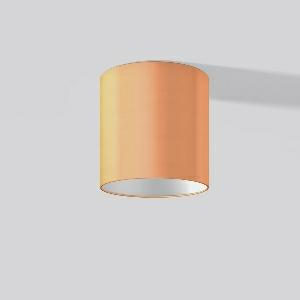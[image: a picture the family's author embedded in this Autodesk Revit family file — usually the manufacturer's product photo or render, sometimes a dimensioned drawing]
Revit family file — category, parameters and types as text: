
# Revit family: toledo_flatliner_901630_002_1_76_9910
name_source: partatom
category: Lighting Fixtures
units: mm (PartAtom-declared; Revit-internal decimal feet)

## family parameters
Cut with Voids When Loaded = No
Host = Face
Light Source = No
Part Type = Normal
Room Calculation Point = No
Round Connector Dimension = Use Diameter
Shared = No

## types (1)
- 982300.002 (1 x LED Modul 840, 660 lm, 4000)
    Apparent Load = 8 VA
    CIE Flux Codes = 56 78 92 81 100
    Color Rendering = 80
    Color Temperature = 4000
    Default Elevation = 1800 mm
    Description = Series: TOLEDO FLATLINER
Decorative ceiling luminaire for interior decoration. Base luminaire prepared for the installation of fabric lampshade. Cylinder housing sheet steel, powder-coated. Housing: die cast aluminium and sheet steel, powder-coated. Bezel ring: die-cast aluminium, powder-coated. Lightguide and diffuser made of non-yellowing plastic (PMMA) opal matt. Modular design: With the basic luminaire, a square or cylindrical fabric lampshade must always be ordered separately. Fabric lampshades can be fitted to the basic luminaire without tools. Order satin finish diffuser as separate accessory. 
Colour: white
Diameter: 202 mm
Height: 65 mm
Lamp: LED
Socket: without socket
Colour temperature: 4000K
Colour rendering index (CRI): 80
System power: 7.7 W
Rated luminous flux: 660 lm
Luminous efficiency: 86 lm/W
Control gear: Converter, dimmable, DALI
Protection class: II
Type of protection: IP 40
    Height = 65 mm
    Lamp = 1 x LED Modul 840
    Lamp Light Flux = 660 lm
    Lamp count = 1
    Length = 202 mm
    Lifetime = 50000 h
    Luminous efficacy = 86 lm/W
    Manufacturer = RZB
    ModVariant = No
    Model = 901630.002.1.76
    Mounting Place = Ceiling
    Mounting Type = Surface mounted
    Number of Poles = 1
    OnlyDefault = Yes
    Power Factor = 1
    Product Name = TOLEDO FLATLINER
    Product group = Surface mounted ceiling Fabric lampshade luminaires
    ProductGroupID = 313
    Protection Class = Protection class II
    Protection Degree = IP 40
    RLX_Detail_Level = 1
    RLX_Emergency_Light_Flux = 0 lm
    RLX_Emergency_Type = 0
    RLX_Emergency_Type_DB = No
    RlxData = <blob elided: 62553 chars, md5=f79855a0>
    Socket = socket
    Standby Power = 0 W
    System Light Flux = 660 lm
    System Power = 8 W
    Type Image = toledo_flatliner_anbau_rund_orange_odeckel.jpg
    URL = http://relux.com
    VarID = 982300_002_5a54
    Voltage = 230 V
    Voltage Range = 220-240 V
    Weight = 0.00 kg
    Width = 0 mm  [stored 0 ft]

note: [stored X ft] marks values corroborated as IEEE doubles in the binary element streams (Revit-internal decimal feet)

## geometry (parser evidence)
native form markers: Blend x4, Sweep x12
no freeform markers — native parametric forms only
